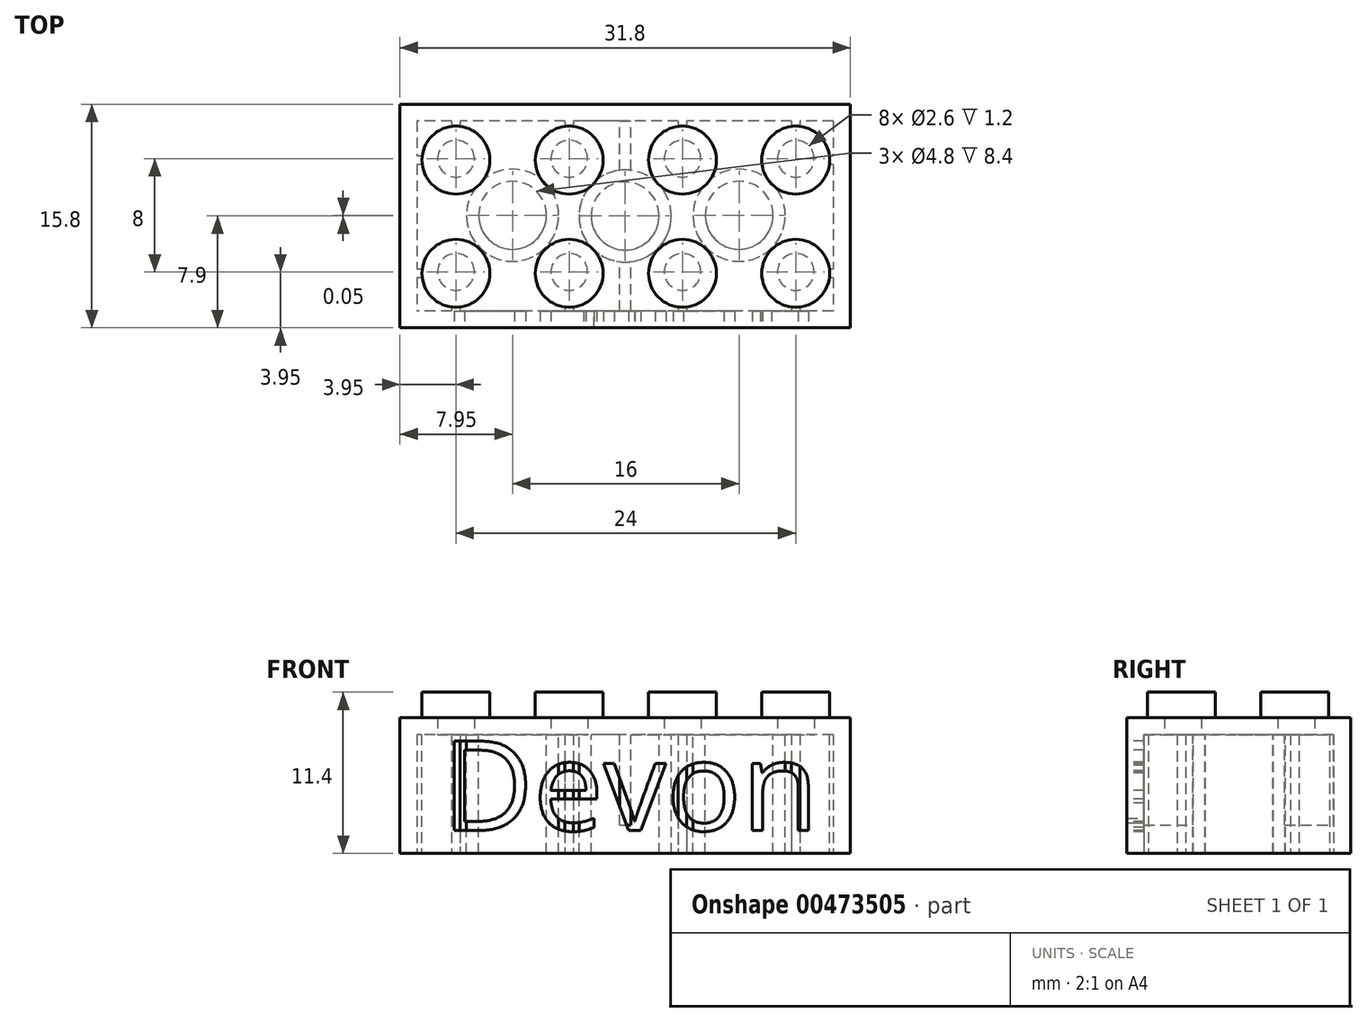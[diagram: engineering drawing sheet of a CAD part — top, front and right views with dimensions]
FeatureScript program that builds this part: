
annotation { "Feature Type Name" : "Feature", "Feature Type Description" : "" }
export const myFeature = defineFeature(function(context is Context, id is Id, definition is map)
    precondition{}
    {
        {
            var Q0;
            Q0=qCreatedBy(makeId("Top.planeOp"),FACE);
            var sketch = newSketch(context, id + "F0", { "sketchPlane" : qUnion([Q0])});
            skLineSegment(sketch, "E0.rect.bottom", {"start": v(-15.9, 7.9) * mm, "end": v(15.9, 7.9) * mm});
            skLineSegment(sketch, "E0.rect.top", {"start": v(-15.9, -7.9) * mm, "end": v(15.9, -7.9) * mm});
            skLineSegment(sketch, "E0.rect.left", {"start": v(-15.9, 7.9) * mm, "end": v(-15.9, -7.9) * mm});
            skLineSegment(sketch, "E0.rect.right", {"start": v(15.9, 7.9) * mm, "end": v(15.9, -7.9) * mm});
            skPoint(sketch, "E0.rect.middle", {"position": v(0, 0) * mm});
            skSolve(sketch);
        }
        {
            var Q0;
            Q0=qSketchRegion(id+"F0",true);
            extrude(context, id + "F1", {"entities" : qUnion([Q0]), "depth" : 9.6 * mm});
        }
        {
            var Q0;
            Q0=makeQuery(id+"F1.opExtrude","CAP_FACE",FACE,{"disambiguationData":[OSD([sQuery(id+"F0.wireOp",EDGE,"E0.rect.bottom"),sQuery(id+"F0.wireOp",EDGE,"E0.rect.top"),sQuery(id+"F0.wireOp",EDGE,"E0.rect.left"),sQuery(id+"F0.wireOp",EDGE,"E0.rect.right")])],"isStart":true});
            var sketch = newSketch(context, id + "F2", { "sketchPlane" : qUnion([Q0])});
            skLineSegment(sketch, "E1.rect.bottom", {"start": v(14.7, -6.7) * mm, "end": v(-14.7, -6.7) * mm});
            skLineSegment(sketch, "E1.rect.top", {"start": v(14.7, 6.7) * mm, "end": v(-14.7, 6.7) * mm});
            skLineSegment(sketch, "E1.rect.left", {"start": v(14.7, -6.7) * mm, "end": v(14.7, 6.7) * mm});
            skLineSegment(sketch, "E1.rect.right", {"start": v(-14.7, -6.7) * mm, "end": v(-14.7, 6.7) * mm});
            skPoint(sketch, "E1.rect.middle", {"position": v(0, 0) * mm});
            skSolve(sketch);
        }
        {
            var Q0;
            Q0=qSketchRegion(id+"F2",true);
            extrude(context, id + "F3", {"entities" : qUnion([Q0]), "operationType" : NewBodyOperationType.REMOVE, "oppositeDirection" : true, "depth" : 8.4 * mm});
        }
        {
            var Q0;
            Q0=makeQuery(id+"F1.opExtrude","CAP_FACE",FACE,{"disambiguationData":[OSD([sQuery(id+"F0.wireOp",EDGE,"E0.rect.bottom"),sQuery(id+"F0.wireOp",EDGE,"E0.rect.top"),sQuery(id+"F0.wireOp",EDGE,"E0.rect.left"),sQuery(id+"F0.wireOp",EDGE,"E0.rect.right")])],"isStart":false});
            var sketch = newSketch(context, id + "F4", { "sketchPlane" : qUnion([Q0])});
            skLineSegment(sketch, "E2", {"start": v(-28.6, 0) * mm, "end": v(26.98, 0) * mm, "construction": true});
            skCircle(sketch, "E3", {"center": v(-11.95, 3.95) * mm, "radius": 2.4 * mm});
            skCircle(sketch, "E4.0.1.0", {"center": v(-11.95, -4.05) * mm, "radius": 2.4 * mm});
            skCircle(sketch, "E4.1.0.0", {"center": v(-3.95, 3.95) * mm, "radius": 2.4 * mm});
            skCircle(sketch, "E4.1.1.0", {"center": v(-3.95, -4.05) * mm, "radius": 2.4 * mm});
            skCircle(sketch, "E4.2.0.0", {"center": v(4.05, 3.95) * mm, "radius": 2.4 * mm});
            skCircle(sketch, "E4.2.1.0", {"center": v(4.05, -4.05) * mm, "radius": 2.4 * mm});
            skCircle(sketch, "E4.3.0.0", {"center": v(12.05, 3.95) * mm, "radius": 2.4 * mm});
            skCircle(sketch, "E4.3.1.0", {"center": v(12.05, -4.05) * mm, "radius": 2.4 * mm});
            skLineSegment(sketch, "E4.direction1", {"start": v(-11.95, 3.95) * mm, "end": v(-3.95, 3.95) * mm, "construction": true});
            skLineSegment(sketch, "E4.direction2", {"start": v(-11.95, 3.95) * mm, "end": v(-11.95, -4.05) * mm, "construction": true});
            skSolve(sketch);
        }
        {
            var Q0;
            Q0=qSketchRegion(id+"F4",true);
            extrude(context, id + "F5", {"entities" : qUnion([Q0]), "operationType" : NewBodyOperationType.ADD, "depth" : 1.8 * mm});
        }
        {
            var Q0;
            Q0=makeQuery(id+"F3.boolean.opBoolean","COPY",FACE,{"derivedFrom":makeQuery(id+"F3.opExtrude","CAP_FACE",FACE,{"disambiguationData":[OSD([sQuery(id+"F2.wireOp",EDGE,"E1.rect.bottom"),sQuery(id+"F2.wireOp",EDGE,"E1.rect.top"),sQuery(id+"F2.wireOp",EDGE,"E1.rect.left"),sQuery(id+"F2.wireOp",EDGE,"E1.rect.right")])],"isStart":false})});
            var sketch = newSketch(context, id + "F6", { "sketchPlane" : qUnion([Q0])});
            skCircle(sketch, "E5", {"center": v(-11.95, 3.95) * mm, "radius": 1.3 * mm});
            skCircle(sketch, "E6.0.1.0", {"center": v(-11.95, -4.05) * mm, "radius": 1.3 * mm});
            skCircle(sketch, "E6.1.0.0", {"center": v(-3.95, 3.95) * mm, "radius": 1.3 * mm});
            skCircle(sketch, "E6.1.1.0", {"center": v(-3.95, -4.05) * mm, "radius": 1.3 * mm});
            skCircle(sketch, "E6.2.0.0", {"center": v(4.05, 3.95) * mm, "radius": 1.3 * mm});
            skCircle(sketch, "E6.2.1.0", {"center": v(4.05, -4.05) * mm, "radius": 1.3 * mm});
            skCircle(sketch, "E6.3.0.0", {"center": v(12.05, 3.95) * mm, "radius": 1.3 * mm});
            skCircle(sketch, "E6.3.1.0", {"center": v(12.05, -4.05) * mm, "radius": 1.3 * mm});
            skLineSegment(sketch, "E6.direction1", {"start": v(-11.95, 3.95) * mm, "end": v(-3.95, 3.95) * mm, "construction": true});
            skLineSegment(sketch, "E6.direction2", {"start": v(-11.95, 3.95) * mm, "end": v(-11.95, -4.05) * mm, "construction": true});
            skSolve(sketch);
        }
        {
            var Q0;
            Q0=qSketchRegion(id+"F6",true);
            extrude(context, id + "F7", {"entities" : qUnion([Q0]), "operationType" : NewBodyOperationType.REMOVE, "oppositeDirection" : true, "depth" : 1.2 * mm});
        }
        {
            var Q0;
            Q0=makeQuery(id+"F3.boolean.opBoolean","COPY",FACE,{"derivedFrom":makeQuery(id+"F3.opExtrude","CAP_FACE",FACE,{"disambiguationData":[OSD([sQuery(id+"F2.wireOp",EDGE,"E1.rect.bottom"),sQuery(id+"F2.wireOp",EDGE,"E1.rect.top"),sQuery(id+"F2.wireOp",EDGE,"E1.rect.left"),sQuery(id+"F2.wireOp",EDGE,"E1.rect.right")])],"isStart":false})});
            var sketch = newSketch(context, id + "F8", { "sketchPlane" : qUnion([Q0])});
            skLineSegment(sketch, "E7", {"start": v(-11.95, 3.95) * mm, "end": v(-3.95, -4.05) * mm, "construction": true});
            skLineSegment(sketch, "E8", {"start": v(-3.95, 3.95) * mm, "end": v(-11.95, -4.05) * mm, "construction": true});
            skLineSegment(sketch, "E9", {"start": v(4.05, 3.95) * mm, "end": v(12.05, -4.05) * mm, "construction": true});
            skLineSegment(sketch, "E10", {"start": v(4.05, -4.05) * mm, "end": v(12.05, 3.95) * mm, "construction": true});
            skLineSegment(sketch, "E11", {"start": v(-3.95, 3.95) * mm, "end": v(4.05, -4.05) * mm, "construction": true});
            skLineSegment(sketch, "E12", {"start": v(4.05, 3.95) * mm, "end": v(-3.95, -4.05) * mm, "construction": true});
            skPoint(sketch, "E13", {"position": v(-7.95, -0.05) * mm});
            skPoint(sketch, "E14", {"position": v(8.05, -0.05) * mm});
            skCircle(sketch, "E15", {"center": v(-7.95, -0.05) * mm, "radius": 2.4 * mm});
            skCircle(sketch, "E16", {"center": v(-7.95, -0.05) * mm, "radius": 3.25 * mm});
            skCircle(sketch, "E17", {"center": v(0, 0) * mm, "radius": 2.4 * mm});
            skCircle(sketch, "E18", {"center": v(0, 0) * mm, "radius": 3.25 * mm});
            skCircle(sketch, "E19", {"center": v(8.05, -0.05) * mm, "radius": 2.4 * mm});
            skCircle(sketch, "E20", {"center": v(8.05, -0.05) * mm, "radius": 3.25 * mm});
            skSolve(sketch);
        }
        {
            var Q0;
            Q0=qSketchRegion(id+"F8",true);
            var Q1;
            Q1=makeQuery(id+"F1.opExtrude","CAP_FACE",FACE,{"disambiguationData":[OSD([sQuery(id+"F0.wireOp",EDGE,"E0.rect.bottom"),sQuery(id+"F0.wireOp",EDGE,"E0.rect.top"),sQuery(id+"F0.wireOp",EDGE,"E0.rect.left"),sQuery(id+"F0.wireOp",EDGE,"E0.rect.right")])],"isStart":true});
            extrude(context, id + "F9", {"entities" : qUnion([Q0]), "operationType" : NewBodyOperationType.ADD, "endBound" : BoundingType.UP_TO_SURFACE, "endBoundEntityFace" : qUnion([Q1]), "depth" : 25 * mm});
        }
        {
            var Q0;
            Q0=makeQuery(id+"F1.opExtrude","CAP_FACE",FACE,{"disambiguationData":[OSD([sQuery(id+"F0.wireOp",EDGE,"E0.rect.bottom"),sQuery(id+"F0.wireOp",EDGE,"E0.rect.top"),sQuery(id+"F0.wireOp",EDGE,"E0.rect.left"),sQuery(id+"F0.wireOp",EDGE,"E0.rect.right")])],"isStart":true});
            var sketch = newSketch(context, id + "F10", { "sketchPlane" : qUnion([Q0])});
            skLineSegment(sketch, "E21.bottom", {"start": v(-12.25, 6.7) * mm, "end": v(-11.65, 6.7) * mm});
            skLineSegment(sketch, "E21.top", {"start": v(-12.25, 6.4) * mm, "end": v(-11.65, 6.4) * mm});
            skLineSegment(sketch, "E21.left", {"start": v(-12.25, 6.7) * mm, "end": v(-12.25, 6.4) * mm});
            skLineSegment(sketch, "E21.right", {"start": v(-11.65, 6.7) * mm, "end": v(-11.65, 6.4) * mm});
            skLineSegment(sketch, "E22", {"start": v(-11.95, 15.64) * mm, "end": v(-11.95, -3.95) * mm, "construction": true});
            skLineSegment(sketch, "E23.0.1.0", {"start": v(-12.25, -6.7) * mm, "end": v(-11.65, -6.7) * mm});
            skLineSegment(sketch, "E23.0.1.1", {"start": v(-12.25, -6.4) * mm, "end": v(-11.65, -6.4) * mm});
            skLineSegment(sketch, "E23.0.1.2", {"start": v(-11.65, -6.4) * mm, "end": v(-11.65, -6.7) * mm});
            skLineSegment(sketch, "E23.0.1.3", {"start": v(-12.25, -6.4) * mm, "end": v(-12.25, -6.7) * mm});
            skLineSegment(sketch, "E23.1.0.0", {"start": v(-4.25, 6.4) * mm, "end": v(-3.65, 6.4) * mm});
            skLineSegment(sketch, "E23.1.0.1", {"start": v(-4.25, 6.7) * mm, "end": v(-3.65, 6.7) * mm});
            skLineSegment(sketch, "E23.1.0.2", {"start": v(-3.65, 6.7) * mm, "end": v(-3.65, 6.4) * mm});
            skLineSegment(sketch, "E23.1.0.3", {"start": v(-4.25, 6.7) * mm, "end": v(-4.25, 6.4) * mm});
            skLineSegment(sketch, "E23.1.1.0", {"start": v(-4.25, -6.7) * mm, "end": v(-3.65, -6.7) * mm});
            skLineSegment(sketch, "E23.1.1.1", {"start": v(-4.25, -6.4) * mm, "end": v(-3.65, -6.4) * mm});
            skLineSegment(sketch, "E23.1.1.2", {"start": v(-3.65, -6.4) * mm, "end": v(-3.65, -6.7) * mm});
            skLineSegment(sketch, "E23.1.1.3", {"start": v(-4.25, -6.4) * mm, "end": v(-4.25, -6.7) * mm});
            skLineSegment(sketch, "E23.2.0.0", {"start": v(3.75, 6.4) * mm, "end": v(4.35, 6.4) * mm});
            skLineSegment(sketch, "E23.2.0.1", {"start": v(3.75, 6.7) * mm, "end": v(4.35, 6.7) * mm});
            skLineSegment(sketch, "E23.2.0.2", {"start": v(4.35, 6.7) * mm, "end": v(4.35, 6.4) * mm});
            skLineSegment(sketch, "E23.2.0.3", {"start": v(3.75, 6.7) * mm, "end": v(3.75, 6.4) * mm});
            skLineSegment(sketch, "E23.2.1.0", {"start": v(3.75, -6.7) * mm, "end": v(4.35, -6.7) * mm});
            skLineSegment(sketch, "E23.2.1.1", {"start": v(3.75, -6.4) * mm, "end": v(4.35, -6.4) * mm});
            skLineSegment(sketch, "E23.2.1.2", {"start": v(4.35, -6.4) * mm, "end": v(4.35, -6.7) * mm});
            skLineSegment(sketch, "E23.2.1.3", {"start": v(3.75, -6.4) * mm, "end": v(3.75, -6.7) * mm});
            skLineSegment(sketch, "E23.3.0.0", {"start": v(11.75, 6.4) * mm, "end": v(12.35, 6.4) * mm});
            skLineSegment(sketch, "E23.3.0.1", {"start": v(11.75, 6.7) * mm, "end": v(12.35, 6.7) * mm});
            skLineSegment(sketch, "E23.3.0.2", {"start": v(12.35, 6.7) * mm, "end": v(12.35, 6.4) * mm});
            skLineSegment(sketch, "E23.3.0.3", {"start": v(11.75, 6.7) * mm, "end": v(11.75, 6.4) * mm});
            skLineSegment(sketch, "E23.3.1.0", {"start": v(11.75, -6.7) * mm, "end": v(12.35, -6.7) * mm});
            skLineSegment(sketch, "E23.3.1.1", {"start": v(11.75, -6.4) * mm, "end": v(12.35, -6.4) * mm});
            skLineSegment(sketch, "E23.3.1.2", {"start": v(12.35, -6.4) * mm, "end": v(12.35, -6.7) * mm});
            skLineSegment(sketch, "E23.3.1.3", {"start": v(11.75, -6.4) * mm, "end": v(11.75, -6.7) * mm});
            skLineSegment(sketch, "E23.direction1", {"start": v(-12.25, 6.4) * mm, "end": v(-4.25, 6.4) * mm, "construction": true});
            skLineSegment(sketch, "E23.direction2", {"start": v(-12.25, 6.4) * mm, "end": v(-12.25, -6.7) * mm, "construction": true});
            skSolve(sketch);
        }
        {
            var Q0;
            Q0=qSketchRegion(id+"F10",true);
            var Q1;
            {var subQ0=sQuery(id+"F2.wireOp",EDGE,"E1.rect.bottom");var subQ1=sQuery(id+"F2.wireOp",EDGE,"E1.rect.top");var subQ2=sQuery(id+"F2.wireOp",EDGE,"E1.rect.left");var subQ3=sQuery(id+"F2.wireOp",EDGE,"E1.rect.right");Q1=makeQuery(id+"F9.boolean.opBoolean","SPLIT",FACE,{"disambiguationData":[TD([makeQuery(id+"F3.boolean.opBoolean","COPY",FACE,{"derivedFrom":makeQuery(id+"F3.opExtrude","SWEPT_FACE",FACE,{"disambiguationData":[OSD([subQ0])]})})])],"derivedFrom":makeQuery(id+"F3.boolean.opBoolean","COPY",FACE,{"derivedFrom":makeQuery(id+"F3.opExtrude","CAP_FACE",FACE,{"disambiguationData":[OSD([subQ0,subQ1,subQ2,subQ3])],"isStart":false})})});}
            extrude(context, id + "F11", {"entities" : qUnion([Q0]), "operationType" : NewBodyOperationType.ADD, "endBound" : BoundingType.UP_TO_SURFACE, "oppositeDirection" : true, "endBoundEntityFace" : qUnion([Q1]), "depth" : 25 * mm});
        }
        {
            var Q0;
            Q0=makeQuery(id+"F11.boolean.opBoolean","MERGE",FACE,{"derivedFrom":[makeQuery(id+"F1.opExtrude","CAP_FACE",FACE,{"disambiguationData":[OSD([sQuery(id+"F0.wireOp",EDGE,"E0.rect.bottom"),sQuery(id+"F0.wireOp",EDGE,"E0.rect.top"),sQuery(id+"F0.wireOp",EDGE,"E0.rect.left"),sQuery(id+"F0.wireOp",EDGE,"E0.rect.right")])],"isStart":true}),makeQuery(id+"F11.opExtrude","CAP_FACE",FACE,{"disambiguationData":[OSD([sQuery(id+"F10.wireOp",EDGE,"E21.bottom"),sQuery(id+"F10.wireOp",EDGE,"E21.top"),sQuery(id+"F10.wireOp",EDGE,"E21.left"),sQuery(id+"F10.wireOp",EDGE,"E21.right")])],"isStart":true}),makeQuery(id+"F11.opExtrude","CAP_FACE",FACE,{"disambiguationData":[OSD([sQuery(id+"F10.wireOp",EDGE,"E23.0.1.0"),sQuery(id+"F10.wireOp",EDGE,"E23.0.1.1"),sQuery(id+"F10.wireOp",EDGE,"E23.0.1.2"),sQuery(id+"F10.wireOp",EDGE,"E23.0.1.3")])],"isStart":true}),makeQuery(id+"F11.opExtrude","CAP_FACE",FACE,{"disambiguationData":[OSD([sQuery(id+"F10.wireOp",EDGE,"E23.1.0.0"),sQuery(id+"F10.wireOp",EDGE,"E23.1.0.1"),sQuery(id+"F10.wireOp",EDGE,"E23.1.0.2"),sQuery(id+"F10.wireOp",EDGE,"E23.1.0.3")])],"isStart":true}),makeQuery(id+"F11.opExtrude","CAP_FACE",FACE,{"disambiguationData":[OSD([sQuery(id+"F10.wireOp",EDGE,"E23.1.1.0"),sQuery(id+"F10.wireOp",EDGE,"E23.1.1.1"),sQuery(id+"F10.wireOp",EDGE,"E23.1.1.2"),sQuery(id+"F10.wireOp",EDGE,"E23.1.1.3")])],"isStart":true}),makeQuery(id+"F11.opExtrude","CAP_FACE",FACE,{"disambiguationData":[OSD([sQuery(id+"F10.wireOp",EDGE,"E23.2.0.0"),sQuery(id+"F10.wireOp",EDGE,"E23.2.0.1"),sQuery(id+"F10.wireOp",EDGE,"E23.2.0.2"),sQuery(id+"F10.wireOp",EDGE,"E23.2.0.3")])],"isStart":true}),makeQuery(id+"F11.opExtrude","CAP_FACE",FACE,{"disambiguationData":[OSD([sQuery(id+"F10.wireOp",EDGE,"E23.2.1.0"),sQuery(id+"F10.wireOp",EDGE,"E23.2.1.1"),sQuery(id+"F10.wireOp",EDGE,"E23.2.1.2"),sQuery(id+"F10.wireOp",EDGE,"E23.2.1.3")])],"isStart":true}),makeQuery(id+"F11.opExtrude","CAP_FACE",FACE,{"disambiguationData":[OSD([sQuery(id+"F10.wireOp",EDGE,"E23.3.0.0"),sQuery(id+"F10.wireOp",EDGE,"E23.3.0.1"),sQuery(id+"F10.wireOp",EDGE,"E23.3.0.2"),sQuery(id+"F10.wireOp",EDGE,"E23.3.0.3")])],"isStart":true}),makeQuery(id+"F11.opExtrude","CAP_FACE",FACE,{"disambiguationData":[OSD([sQuery(id+"F10.wireOp",EDGE,"E23.3.1.0"),sQuery(id+"F10.wireOp",EDGE,"E23.3.1.1"),sQuery(id+"F10.wireOp",EDGE,"E23.3.1.2"),sQuery(id+"F10.wireOp",EDGE,"E23.3.1.3")])],"isStart":true})]});
            var sketch = newSketch(context, id + "F12", { "sketchPlane" : qUnion([Q0])});
            skLineSegment(sketch, "E24", {"start": v(-21.2, 4.05) * mm, "end": v(-11.95, 4.05) * mm, "construction": true});
            skLineSegment(sketch, "E25.bottom", {"start": v(-14.7, 4.35) * mm, "end": v(-14.4, 4.35) * mm});
            skLineSegment(sketch, "E25.top", {"start": v(-14.7, 3.75) * mm, "end": v(-14.4, 3.75) * mm});
            skLineSegment(sketch, "E25.left", {"start": v(-14.7, 4.35) * mm, "end": v(-14.7, 3.75) * mm});
            skLineSegment(sketch, "E25.right", {"start": v(-14.4, 4.35) * mm, "end": v(-14.4, 3.75) * mm});
            skLineSegment(sketch, "E26.0.1.0", {"start": v(-14.7, -4.25) * mm, "end": v(-14.4, -4.25) * mm});
            skLineSegment(sketch, "E26.0.1.1", {"start": v(-14.7, -3.65) * mm, "end": v(-14.7, -4.25) * mm});
            skLineSegment(sketch, "E26.0.1.2", {"start": v(-14.7, -3.65) * mm, "end": v(-14.4, -3.65) * mm});
            skLineSegment(sketch, "E26.0.1.3", {"start": v(-14.4, -3.65) * mm, "end": v(-14.4, -4.25) * mm});
            skLineSegment(sketch, "E26.1.0.0", {"start": v(14.4, 3.75) * mm, "end": v(14.7, 3.75) * mm});
            skLineSegment(sketch, "E26.1.0.1", {"start": v(14.4, 4.35) * mm, "end": v(14.4, 3.75) * mm});
            skLineSegment(sketch, "E26.1.0.2", {"start": v(14.4, 4.35) * mm, "end": v(14.7, 4.35) * mm});
            skLineSegment(sketch, "E26.1.0.3", {"start": v(14.7, 4.35) * mm, "end": v(14.7, 3.75) * mm});
            skLineSegment(sketch, "E26.1.1.0", {"start": v(14.4, -4.25) * mm, "end": v(14.7, -4.25) * mm});
            skLineSegment(sketch, "E26.1.1.1", {"start": v(14.4, -3.65) * mm, "end": v(14.4, -4.25) * mm});
            skLineSegment(sketch, "E26.1.1.2", {"start": v(14.4, -3.65) * mm, "end": v(14.7, -3.65) * mm});
            skLineSegment(sketch, "E26.1.1.3", {"start": v(14.7, -3.65) * mm, "end": v(14.7, -4.25) * mm});
            skLineSegment(sketch, "E26.direction1", {"start": v(-14.7, 3.75) * mm, "end": v(14.4, 3.75) * mm, "construction": true});
            skLineSegment(sketch, "E26.direction2", {"start": v(-14.7, 3.75) * mm, "end": v(-14.7, -4.25) * mm, "construction": true});
            skSolve(sketch);
        }
        {
            var Q0;
            Q0=qSketchRegion(id+"F12",true);
            var Q1;
            {var subQ0=sQuery(id+"F2.wireOp",EDGE,"E1.rect.bottom");var subQ1=sQuery(id+"F2.wireOp",EDGE,"E1.rect.top");var subQ2=sQuery(id+"F2.wireOp",EDGE,"E1.rect.left");var subQ3=sQuery(id+"F2.wireOp",EDGE,"E1.rect.right");Q1=makeQuery(id+"F9.boolean.opBoolean","SPLIT",FACE,{"disambiguationData":[TD([makeQuery(id+"F3.boolean.opBoolean","COPY",FACE,{"derivedFrom":makeQuery(id+"F3.opExtrude","SWEPT_FACE",FACE,{"disambiguationData":[OSD([subQ0])]})})])],"derivedFrom":makeQuery(id+"F3.boolean.opBoolean","COPY",FACE,{"derivedFrom":makeQuery(id+"F3.opExtrude","CAP_FACE",FACE,{"disambiguationData":[OSD([subQ0,subQ1,subQ2,subQ3])],"isStart":false})})});}
            extrude(context, id + "F13", {"entities" : qUnion([Q0]), "operationType" : NewBodyOperationType.ADD, "endBound" : BoundingType.UP_TO_SURFACE, "oppositeDirection" : true, "endBoundEntityFace" : qUnion([Q1]), "depth" : 25 * mm});
        }
        {
            var Q0;
            {var subQ0=sQuery(id+"F2.wireOp",EDGE,"E1.rect.bottom");var subQ1=sQuery(id+"F2.wireOp",EDGE,"E1.rect.top");var subQ2=sQuery(id+"F2.wireOp",EDGE,"E1.rect.left");var subQ3=sQuery(id+"F2.wireOp",EDGE,"E1.rect.right");Q0=makeQuery(id+"F9.boolean.opBoolean","SPLIT",FACE,{"disambiguationData":[TD([makeQuery(id+"F3.boolean.opBoolean","COPY",FACE,{"derivedFrom":makeQuery(id+"F3.opExtrude","SWEPT_FACE",FACE,{"disambiguationData":[OSD([subQ0])]})})])],"derivedFrom":makeQuery(id+"F3.boolean.opBoolean","COPY",FACE,{"derivedFrom":makeQuery(id+"F3.opExtrude","CAP_FACE",FACE,{"disambiguationData":[OSD([subQ0,subQ1,subQ2,subQ3])],"isStart":false})})});}
            var sketch = newSketch(context, id + "F14", { "sketchPlane" : qUnion([Q0])});
            skLineSegment(sketch, "E27.bottom", {"start": v(-0.4, 6.9) * mm, "end": v(0.4, 6.9) * mm});
            skLineSegment(sketch, "E27.top", {"start": v(-0.4, 3.1) * mm, "end": v(0.4, 3.1) * mm});
            skLineSegment(sketch, "E27.left", {"start": v(-0.4, 6.9) * mm, "end": v(-0.4, 3.1) * mm});
            skLineSegment(sketch, "E27.right", {"start": v(0.4, 6.9) * mm, "end": v(0.4, 3.1) * mm});
            skLineSegment(sketch, "E28.bottom", {"start": v(-0.4, -3.1) * mm, "end": v(0.4, -3.1) * mm});
            skLineSegment(sketch, "E28.top", {"start": v(-0.4, -6.9) * mm, "end": v(0.4, -6.9) * mm});
            skLineSegment(sketch, "E28.left", {"start": v(-0.4, -3.1) * mm, "end": v(-0.4, -6.9) * mm});
            skLineSegment(sketch, "E28.right", {"start": v(0.4, -3.1) * mm, "end": v(0.4, -6.9) * mm});
            skSolve(sketch);
        }
        {
            var Q0;
            Q0=qSketchRegion(id+"F14",true);
            var Q1;
            Q1=makeQuery(id+"F13.boolean.opBoolean","MERGE",FACE,{"derivedFrom":[makeQuery(id+"F11.boolean.opBoolean","MERGE",FACE,{"derivedFrom":[makeQuery(id+"F1.opExtrude","CAP_FACE",FACE,{"disambiguationData":[OSD([sQuery(id+"F0.wireOp",EDGE,"E0.rect.bottom"),sQuery(id+"F0.wireOp",EDGE,"E0.rect.top"),sQuery(id+"F0.wireOp",EDGE,"E0.rect.left"),sQuery(id+"F0.wireOp",EDGE,"E0.rect.right")])],"isStart":true}),makeQuery(id+"F11.opExtrude","CAP_FACE",FACE,{"disambiguationData":[OSD([sQuery(id+"F10.wireOp",EDGE,"E21.bottom"),sQuery(id+"F10.wireOp",EDGE,"E21.top"),sQuery(id+"F10.wireOp",EDGE,"E21.left"),sQuery(id+"F10.wireOp",EDGE,"E21.right")])],"isStart":true}),makeQuery(id+"F11.opExtrude","CAP_FACE",FACE,{"disambiguationData":[OSD([sQuery(id+"F10.wireOp",EDGE,"E23.0.1.0"),sQuery(id+"F10.wireOp",EDGE,"E23.0.1.1"),sQuery(id+"F10.wireOp",EDGE,"E23.0.1.2"),sQuery(id+"F10.wireOp",EDGE,"E23.0.1.3")])],"isStart":true}),makeQuery(id+"F11.opExtrude","CAP_FACE",FACE,{"disambiguationData":[OSD([sQuery(id+"F10.wireOp",EDGE,"E23.1.0.0"),sQuery(id+"F10.wireOp",EDGE,"E23.1.0.1"),sQuery(id+"F10.wireOp",EDGE,"E23.1.0.2"),sQuery(id+"F10.wireOp",EDGE,"E23.1.0.3")])],"isStart":true}),makeQuery(id+"F11.opExtrude","CAP_FACE",FACE,{"disambiguationData":[OSD([sQuery(id+"F10.wireOp",EDGE,"E23.1.1.0"),sQuery(id+"F10.wireOp",EDGE,"E23.1.1.1"),sQuery(id+"F10.wireOp",EDGE,"E23.1.1.2"),sQuery(id+"F10.wireOp",EDGE,"E23.1.1.3")])],"isStart":true}),makeQuery(id+"F11.opExtrude","CAP_FACE",FACE,{"disambiguationData":[OSD([sQuery(id+"F10.wireOp",EDGE,"E23.2.0.0"),sQuery(id+"F10.wireOp",EDGE,"E23.2.0.1"),sQuery(id+"F10.wireOp",EDGE,"E23.2.0.2"),sQuery(id+"F10.wireOp",EDGE,"E23.2.0.3")])],"isStart":true}),makeQuery(id+"F11.opExtrude","CAP_FACE",FACE,{"disambiguationData":[OSD([sQuery(id+"F10.wireOp",EDGE,"E23.2.1.0"),sQuery(id+"F10.wireOp",EDGE,"E23.2.1.1"),sQuery(id+"F10.wireOp",EDGE,"E23.2.1.2"),sQuery(id+"F10.wireOp",EDGE,"E23.2.1.3")])],"isStart":true}),makeQuery(id+"F11.opExtrude","CAP_FACE",FACE,{"disambiguationData":[OSD([sQuery(id+"F10.wireOp",EDGE,"E23.3.0.0"),sQuery(id+"F10.wireOp",EDGE,"E23.3.0.1"),sQuery(id+"F10.wireOp",EDGE,"E23.3.0.2"),sQuery(id+"F10.wireOp",EDGE,"E23.3.0.3")])],"isStart":true}),makeQuery(id+"F11.opExtrude","CAP_FACE",FACE,{"disambiguationData":[OSD([sQuery(id+"F10.wireOp",EDGE,"E23.3.1.0"),sQuery(id+"F10.wireOp",EDGE,"E23.3.1.1"),sQuery(id+"F10.wireOp",EDGE,"E23.3.1.2"),sQuery(id+"F10.wireOp",EDGE,"E23.3.1.3")])],"isStart":true})]}),makeQuery(id+"F13.opExtrude","CAP_FACE",FACE,{"disambiguationData":[OSD([sQuery(id+"F12.wireOp",EDGE,"E25.bottom"),sQuery(id+"F12.wireOp",EDGE,"E25.top"),sQuery(id+"F12.wireOp",EDGE,"E25.left"),sQuery(id+"F12.wireOp",EDGE,"E25.right")])],"isStart":true}),makeQuery(id+"F13.opExtrude","CAP_FACE",FACE,{"disambiguationData":[OSD([sQuery(id+"F12.wireOp",EDGE,"E26.0.1.0"),sQuery(id+"F12.wireOp",EDGE,"E26.0.1.1"),sQuery(id+"F12.wireOp",EDGE,"E26.0.1.2"),sQuery(id+"F12.wireOp",EDGE,"E26.0.1.3")])],"isStart":true}),makeQuery(id+"F13.opExtrude","CAP_FACE",FACE,{"disambiguationData":[OSD([sQuery(id+"F12.wireOp",EDGE,"E26.1.0.0"),sQuery(id+"F12.wireOp",EDGE,"E26.1.0.1"),sQuery(id+"F12.wireOp",EDGE,"E26.1.0.2"),sQuery(id+"F12.wireOp",EDGE,"E26.1.0.3")])],"isStart":true}),makeQuery(id+"F13.opExtrude","CAP_FACE",FACE,{"disambiguationData":[OSD([sQuery(id+"F12.wireOp",EDGE,"E26.1.1.0"),sQuery(id+"F12.wireOp",EDGE,"E26.1.1.1"),sQuery(id+"F12.wireOp",EDGE,"E26.1.1.2"),sQuery(id+"F12.wireOp",EDGE,"E26.1.1.3")])],"isStart":true})]});
            extrude(context, id + "F15", {"entities" : qUnion([Q0]), "operationType" : NewBodyOperationType.ADD, "endBoundEntityFace" : qUnion([Q1]), "depth" : 6.4 * mm});
        }
        {
            var Q0;
            Q0=makeQuery(id+"F1.opExtrude","SWEPT_FACE",FACE,{"disambiguationData":[OSD([sQuery(id+"F0.wireOp",EDGE,"E0.rect.top")])]});
            var sketch = newSketch(context, id + "F16", { "sketchPlane" : qUnion([Q0])});
            skText(sketch, "E29", { "text": "Devon", "fontName": "OpenSans-Regular.ttf"});
            const initialGuessF16  = {"E29": [-0.01293, 0.00163, 1, 0, 0.00636]};
            skSetInitialGuess(sketch, initialGuessF16);
            skSolve(sketch);
        }
        {
            var Q0;
            Q0=qSketchRegion(id+"F16",true);
            extrude(context, id + "F17", {"entities" : qUnion([Q0]), "operationType" : NewBodyOperationType.REMOVE, "oppositeDirection" : true, "depth" : 1.2 * mm});
        }
    });
